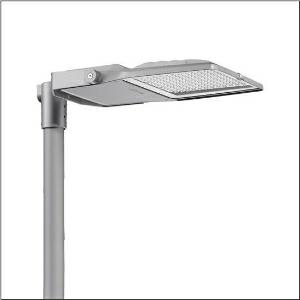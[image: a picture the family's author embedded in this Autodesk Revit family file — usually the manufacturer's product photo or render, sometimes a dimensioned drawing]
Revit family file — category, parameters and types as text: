
# Revit family: floodlight_fl_21_midi___pl33t_5xa7786e2f3a_2de9
name_source: partatom
category: Lighting Fixtures
units: mm (PartAtom-declared; Revit-internal decimal feet)

## family parameters
Cut with Voids When Loaded = No
Host = Face
Light Source = No
Part Type = Normal
Room Calculation Point = No
Round Connector Dimension = Use Diameter
Shared = No

## types (1)
- --- (1 x LED, 26630 lm, 212.4 W, 3000K)
    Apparent Load = 212 VA
    CIE Flux Codes = 26 75 99 100 100
    Color Rendering = 70
    Color Temperature = 3000K
    Default Elevation = 1800 mm
    Description = Floodlight FL 21 midi, floodlight, primary light control with lens, of PMMA, primary optical cover: protective disc, of toughened safety glass, transparent, light distribution: PL33T, light emission: direct distribution, installation type: surface-mounted, LED, High Power LED, rated luminous flux: 26.630lm, luminous efficacy: 125lm/W, light colour: 730, colour temperature: 3000K, control gear: Smart Interface (Zhaga), control: flexible luminous flux parameterisation, time-dependent luminous flux control, constant luminous flux control, overheat protection, pre-setting: logarithmic dimming characteristic, with terminal, 6-pole, mains connection: 220..240V, AC, 50/60Hz, start of lifetime: 212W, end of service life: 231W, reduction: 95W, luminaire housing, of diecast aluminium, powder-coated, Siteco® metallic grey (DB 702S), corrosivity category C5 mid according to DIN EN ISO 12944, suitable for swimming pools, chlorine-resistant, sealing non-destructively replaceable, please order mast flange separately, mast bracket, of steel, galvanised, powder-coated, Siteco® metallic grey (DB 702S), Smart Interface below and above, protection rating (complete): IP66, insulation class (complete): insulation class II (safety insulation), certification: CE, ENEC, VDE, protection symbol: D, impact resistance: IK08, permissible operating ambient temperature: -40..+40°C, permissible operating ambient temperature for outdoor applications: -40..+50°C, standard: DIN EN 12944, LABS conformity tested according to VDMA 24364:2018-05, packaging unit: 1 piece

Light Distribution: PL33T
    Height = 76 mm
    Lamp = 1 x LED
    Lamp Light Flux = 26630 lm
    Lamp Power = 212.4 W
    Lamp count = 1
    Length = 657 mm
    Luminous efficacy = 125 lm/W
    Manufacturer = Siteco
    ModVariant = No
    Model = 5XA7786E2F3A
    Number of Poles = 1
    OnlyDefault = Yes
    Power Factor = 1
    Product Name = Floodlight FL 21 midi | PL33T
    Product group = floodlight | pylon annexe
    ProductGroupID = 6200
    Protection Class = Protection class II
    Protection Degree = IP 66
    RLX_Detail_Level = 1
    RLX_Emergency_Light_Flux = 0 lm
    RLX_Emergency_Type = 0
    RLX_Emergency_Type_DB = No
    RlxData = <blob elided: 153577 chars, md5=e21799de>
    Socket = socket
    Standby Power = 0 W
    System Light Flux = 26630 lm
    System Power = 212 W
    Type Comments = factory setting: luminous flux: 100 % | dim-lin: 254 | 710 mA
    Type Image = l_1007123.jpg
    URL = http://relux.com
    VarID = @adj_150544
    Voltage = 0 V
    Weight = 0.00 kg
    Width = 442 mm

## geometry (parser evidence)
native form markers: Blend x4, Sweep x15
no freeform markers — native parametric forms only
